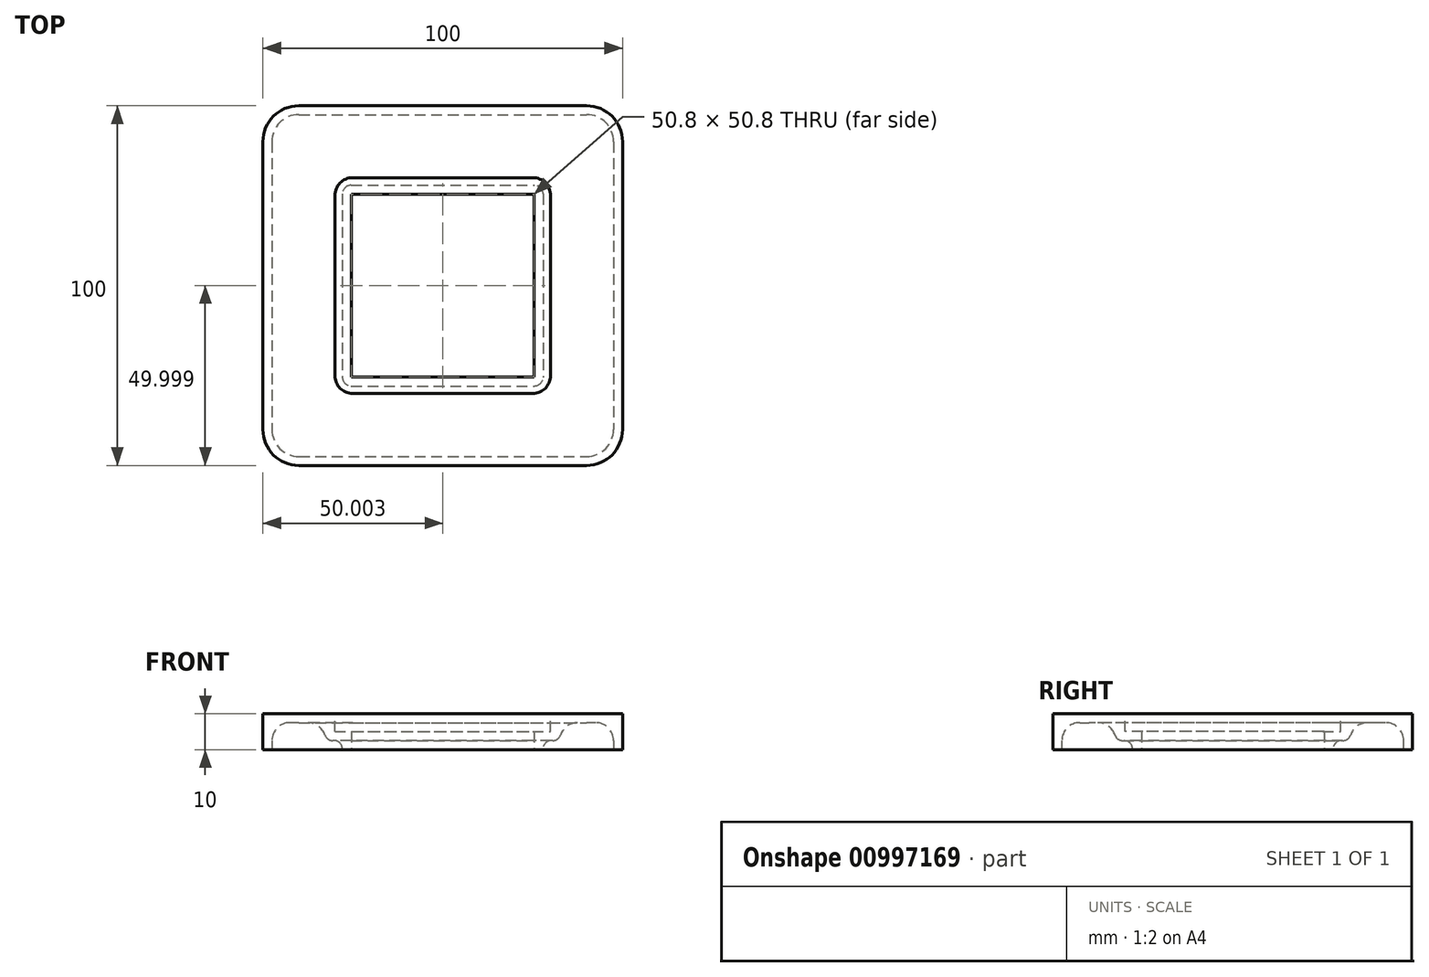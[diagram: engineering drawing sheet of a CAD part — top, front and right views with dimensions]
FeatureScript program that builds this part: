
annotation { "Feature Type Name" : "Feature", "Feature Type Description" : "" }
export const myFeature = defineFeature(function(context is Context, id is Id, definition is map)
    precondition{}
    {
        {
            var Q0;
            Q0=qCreatedBy(makeId("Top.planeOp"),FACE);
            var sketch = newSketch(context, id + "F0", { "sketchPlane" : qUnion([Q0])});
            skLineSegment(sketch, "E0.bottom", {"start": v(-24.48, 28.66) * mm, "end": v(26.32, 28.66) * mm});
            skLineSegment(sketch, "E0.top", {"start": v(-24.48, -22.14) * mm, "end": v(26.32, -22.14) * mm});
            skLineSegment(sketch, "E0.left", {"start": v(-24.48, 28.66) * mm, "end": v(-24.48, -22.14) * mm});
            skLineSegment(sketch, "E0.right", {"start": v(26.32, 28.66) * mm, "end": v(26.32, -22.14) * mm});
            skLineSegment(sketch, "E1.bottom", {"start": v(-49.08, 53.26) * mm, "end": v(50.92, 53.26) * mm});
            skLineSegment(sketch, "E1.top", {"start": v(-49.08, -46.74) * mm, "end": v(50.92, -46.74) * mm});
            skLineSegment(sketch, "E1.left", {"start": v(-49.08, 53.26) * mm, "end": v(-49.08, -46.74) * mm});
            skLineSegment(sketch, "E1.right", {"start": v(50.92, 53.26) * mm, "end": v(50.92, -46.74) * mm});
            skLineSegment(sketch, "E2", {"start": v(-49.08, -46.74) * mm, "end": v(-24.48, -22.14) * mm, "construction": true});
            skLineSegment(sketch, "E3", {"start": v(-49.08, 53.26) * mm, "end": v(-24.48, 28.66) * mm, "construction": true});
            skLineSegment(sketch, "E4", {"start": v(26.32, 28.66) * mm, "end": v(50.92, 53.26) * mm, "construction": true});
            skSolve(sketch);
        }
        {
            var Q0;
            Q0 = qSketchRegion(id + "F0", true);
            extrude(context, id + "F1", {"entities" : qUnion([Q0]), "depth" : 10 * mm, "offsetDistance" : 25 * mm});
        }
        {
            var Q0;
            Q0=makeQuery(id+"F1.opExtrude","CAP_FACE",FACE,{"disambiguationData":[OSD([sQuery(id+"F0.wireOp",EDGE,"E0.bottom"),sQuery(id+"F0.wireOp",EDGE,"E0.top"),sQuery(id+"F0.wireOp",EDGE,"E0.left"),sQuery(id+"F0.wireOp",EDGE,"E0.right"),sQuery(id+"F0.wireOp",EDGE,"E1.bottom"),sQuery(id+"F0.wireOp",EDGE,"E1.top"),sQuery(id+"F0.wireOp",EDGE,"E1.left"),sQuery(id+"F0.wireOp",EDGE,"E1.right")])],"isStart":false});
            var sketch = newSketch(context, id + "F2", { "sketchPlane" : qUnion([Q0])});
            skLineSegment(sketch, "E5.bottom", {"start": v(-29.08, 33.26) * mm, "end": v(30.92, 33.26) * mm});
            skLineSegment(sketch, "E5.top", {"start": v(-29.08, -26.74) * mm, "end": v(30.92, -26.74) * mm});
            skLineSegment(sketch, "E5.left", {"start": v(-29.08, 33.26) * mm, "end": v(-29.08, -26.74) * mm});
            skLineSegment(sketch, "E5.right", {"start": v(30.92, 33.26) * mm, "end": v(30.92, -26.74) * mm});
            skLineSegment(sketch, "E6", {"start": v(-29.08, 33.26) * mm, "end": v(-24.48, 28.66) * mm, "construction": true});
            skLineSegment(sketch, "E7.0", {"start": v(-24.48, 28.66) * mm, "end": v(26.32, 28.66) * mm, "construction": true});
            skLineSegment(sketch, "E8.0", {"start": v(-24.48, 28.66) * mm, "end": v(-24.48, -22.14) * mm, "construction": true});
            skLineSegment(sketch, "E9.0", {"start": v(-24.48, -22.14) * mm, "end": v(26.32, -22.14) * mm, "construction": true});
            skLineSegment(sketch, "E10.0", {"start": v(26.32, 28.66) * mm, "end": v(26.32, -22.14) * mm, "construction": true});
            skLineSegment(sketch, "E11", {"start": v(26.32, 28.66) * mm, "end": v(30.92, 33.26) * mm, "construction": true});
            skLineSegment(sketch, "E12", {"start": v(26.32, -22.14) * mm, "end": v(30.92, -26.74) * mm, "construction": true});
            skSolve(sketch);
        }
        {
            var Q0;
            Q0 = qSketchRegion(id + "F2", true);
            var Q1;
            Q1=sQuery(id+"F2.wireOp",EDGE,"E7.0");
            var Q2;
            Q2=sQuery(id+"F2.wireOp",EDGE,"E8.0");
            var Q3;
            Q3=sQuery(id+"F2.wireOp",EDGE,"E10.0");
            var Q4;
            Q4=sQuery(id+"F2.wireOp",EDGE,"E9.0");
            extrude(context, id + "F3", {"entities" : qUnion([Q0]), "operationType" : NewBodyOperationType.REMOVE, "surfaceEntities" : qUnion([Q1, Q2, Q3, Q4]), "oppositeDirection" : true, "depth" : 5 * mm, "offsetDistance" : 25 * mm});
        }
        {
            var Q0;
            Q0=makeQuery(id+"F1.opExtrude","SWEPT_EDGE",EDGE,{"disambiguationData":[OSD([sQuery(id+"F0.wireOp",EDGE,"E1.top"),sQuery(id+"F0.wireOp",EDGE,"E1.right")])]});
            var Q1;
            Q1=makeQuery(id+"F1.opExtrude","SWEPT_EDGE",EDGE,{"disambiguationData":[OSD([sQuery(id+"F0.wireOp",EDGE,"E1.bottom"),sQuery(id+"F0.wireOp",EDGE,"E1.right")])]});
            var Q2;
            Q2=makeQuery(id+"F1.opExtrude","SWEPT_EDGE",EDGE,{"disambiguationData":[OSD([sQuery(id+"F0.wireOp",EDGE,"E1.bottom"),sQuery(id+"F0.wireOp",EDGE,"E1.left")])]});
            var Q3;
            Q3=makeQuery(id+"F1.opExtrude","SWEPT_EDGE",EDGE,{"disambiguationData":[OSD([sQuery(id+"F0.wireOp",EDGE,"E1.top"),sQuery(id+"F0.wireOp",EDGE,"E1.left")])]});
            fillet(context, id + "F4", {"entities" : qUnion([Q0, Q1, Q2, Q3]), "radius" : 10 * mm, "tangentPropagation" : true, "allowEdgeOverflow" : false});
        }
        {
            var Q0;
            Q0=makeQuery(id+"F3.boolean.opBoolean","COPY",EDGE,{"derivedFrom":makeQuery(id+"F3.opExtrude","SWEPT_EDGE",EDGE,{"disambiguationData":[OSD([sQuery(id+"F2.wireOp",EDGE,"E5.bottom"),sQuery(id+"F2.wireOp",EDGE,"E5.left")])]})});
            var Q1;
            Q1=makeQuery(id+"F3.boolean.opBoolean","COPY",EDGE,{"derivedFrom":makeQuery(id+"F3.opExtrude","SWEPT_EDGE",EDGE,{"disambiguationData":[OSD([sQuery(id+"F2.wireOp",EDGE,"E5.bottom"),sQuery(id+"F2.wireOp",EDGE,"E5.right")])]})});
            var Q2;
            Q2=makeQuery(id+"F3.boolean.opBoolean","COPY",EDGE,{"derivedFrom":makeQuery(id+"F3.opExtrude","SWEPT_EDGE",EDGE,{"disambiguationData":[OSD([sQuery(id+"F2.wireOp",EDGE,"E5.top"),sQuery(id+"F2.wireOp",EDGE,"E5.right")])]})});
            var Q3;
            Q3=makeQuery(id+"F3.boolean.opBoolean","COPY",EDGE,{"derivedFrom":makeQuery(id+"F3.opExtrude","SWEPT_EDGE",EDGE,{"disambiguationData":[OSD([sQuery(id+"F2.wireOp",EDGE,"E5.top"),sQuery(id+"F2.wireOp",EDGE,"E5.left")])]})});
            fillet(context, id + "F5", {"entities" : qUnion([Q0, Q1, Q2, Q3]), "radius" : 5 * mm, "tangentPropagation" : true, "allowEdgeOverflow" : false});
        }
        {
            var Q0;
            Q0=makeQuery(id+"F1.opExtrude","CAP_FACE",FACE,{"disambiguationData":[OSD([sQuery(id+"F0.wireOp",EDGE,"E0.bottom"),sQuery(id+"F0.wireOp",EDGE,"E0.top"),sQuery(id+"F0.wireOp",EDGE,"E0.left"),sQuery(id+"F0.wireOp",EDGE,"E0.right"),sQuery(id+"F0.wireOp",EDGE,"E1.bottom"),sQuery(id+"F0.wireOp",EDGE,"E1.top"),sQuery(id+"F0.wireOp",EDGE,"E1.left"),sQuery(id+"F0.wireOp",EDGE,"E1.right")])],"isStart":true});
            shell(context, id + "F6", {"entities" : qUnion([Q0]), "thickness" : 2.5 * mm});
        }
        {
            var Q0;
            {var subQ0=sQuery(id+"F0.wireOp",EDGE,"E1.right");var subQ1=sQuery(id+"F0.wireOp",EDGE,"E1.left");var subQ2=sQuery(id+"F0.wireOp",EDGE,"E1.top");var subQ3=sQuery(id+"F0.wireOp",EDGE,"E1.bottom");var subQ4=sQuery(id+"F0.wireOp",EDGE,"E0.right");var subQ5=sQuery(id+"F0.wireOp",EDGE,"E0.left");var subQ6=sQuery(id+"F0.wireOp",EDGE,"E0.top");var subQ7=sQuery(id+"F0.wireOp",EDGE,"E0.bottom");Q0=makeQuery(id+"F6.opShell","OFFSET_FACE",FACE,{"disambiguationData":[OSD([subQ7,subQ6,subQ5,subQ4,subQ3,subQ2,subQ1,subQ0]),TDD([makeQuery(id+"F1.opExtrude","CAP_FACE",FACE,{"disambiguationData":[OSD([subQ7,subQ6,subQ5,subQ4,subQ3,subQ2,subQ1,subQ0])],"isStart":false})])]});}
            fillet(context, id + "F7", {"entities" : qUnion([Q0]), "radius" : 5 * mm, "tangentPropagation" : true, "allowEdgeOverflow" : false});
        }
        {
            var Q0;
            Q0=makeQuery(id+"F6.opShell","OFFSET_EDGE",EDGE,{"disambiguationData":[OSD([sQuery(id+"F0.wireOp",EDGE,"E0.top"),sQuery(id+"F0.wireOp",EDGE,"E0.left")])]});
            var Q1;
            Q1=makeQuery(id+"F6.opShell","OFFSET_EDGE",EDGE,{"disambiguationData":[OSD([sQuery(id+"F0.wireOp",EDGE,"E0.bottom"),sQuery(id+"F0.wireOp",EDGE,"E0.left")])]});
            var Q2;
            Q2=makeQuery(id+"F6.opShell","OFFSET_EDGE",EDGE,{"disambiguationData":[OSD([sQuery(id+"F0.wireOp",EDGE,"E0.bottom"),sQuery(id+"F0.wireOp",EDGE,"E0.right")])]});
            var Q3;
            Q3=makeQuery(id+"F6.opShell","OFFSET_EDGE",EDGE,{"disambiguationData":[OSD([sQuery(id+"F0.wireOp",EDGE,"E0.top"),sQuery(id+"F0.wireOp",EDGE,"E0.right")])]});
            fillet(context, id + "F8", {"entities" : qUnion([Q0, Q1, Q2, Q3]), "radius" : 2.41 * mm, "tangentPropagation" : true, "allowEdgeOverflow" : false});
        }
        {
            var Q0;
            Q0=makeQuery(id+"F6.opShell","OFFSET_FACE",FACE,{"disambiguationData":[OSD([sQuery(id+"F2.wireOp",EDGE,"E5.bottom"),sQuery(id+"F2.wireOp",EDGE,"E5.top"),sQuery(id+"F2.wireOp",EDGE,"E5.left"),sQuery(id+"F2.wireOp",EDGE,"E5.right")])]});
            fillet(context, id + "F9", {"entities" : qUnion([Q0]), "radius" : 2.3 * mm, "tangentPropagation" : true, "allowEdgeOverflow" : false});
        }
    });
